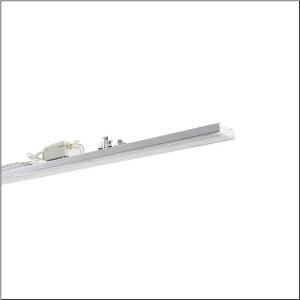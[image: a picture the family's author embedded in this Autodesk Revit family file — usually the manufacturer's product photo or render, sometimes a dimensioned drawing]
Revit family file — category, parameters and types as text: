
# Revit family: licross_r__21_recessed_ho_52te18dn4e5m_8491
name_source: partatom
category: Lighting Fixtures
units: mm (PartAtom-declared; Revit-internal decimal feet)

## family parameters
Cut with Voids When Loaded = No
Host = Face
Light Source = No
Part Type = Normal
Room Calculation Point = No
Round Connector Dimension = Use Diameter
Shared = No

## types (1)
- --- (1 x LED, 14850 lm, 84.6 W, 4000K)
    Apparent Load = 85 VA
    CIE Flux Codes = 75 94 99 100 100
    Color Rendering = 80
    Color Temperature = 4000K
    Default Elevation = 1800 mm
    Description = Licross® 21 Recessed HO, luminaire insert, of sheet steel, galvanised, coil coated, white, length: 1.500mm, width: 66mm, height: 67mm, LED rated luminous flux: 14.850lm, light colour: 840, control gear: DALI 2, with plug, 5-pole, with phase selection, mains connection: 220..240V, AC, 50/60Hz, rated input power: 85W, halogen-free wiring, primary light control with lens, of plastic, primary optical cover: cover, of PMMA, light emission: direct distribution, primary light characteristic: symmetric, protection rating (complete): IP54, insulation class (complete): insulation class I (protective earthing), certification: CE, ENEC, VDE, UKCA, protection symbol: D if used in an environment with non-conductive dust loads with corresponding accessories, impact resistance: IK06, permissible ambient temperature for indoor applications: -25..+30°C, corresponds to IFS (International Featured Standards) requirements for safety and quality in the food industry, reducing of maximum allowable ambient temperature of 5°C with ceiling mounting, LABS conformity tested according to VDMA 24364:2018-05, packaging unit: 1 piece
    Height = 58 mm
    Lamp = 1 x LED
    Lamp Light Flux = 14850 lm
    Lamp Power = 84.6 W
    Lamp count = 1
    Length = 1500 mm
    Luminous efficacy = 176 lm/W
    Manufacturer = Siteco
    ModVariant = No
    Model = 52TE18DN4E5M
    Mounting Place = Ceiling
    Mounting Type = Pendant
    Number of Poles = 1
    OnlyDefault = Yes
    Power Factor = 1
    Product Name = Licross® 21 Recessed HO
    Product group = luminaire insert
    ProductGroupID = 901
    Protection Class = Protection class I
    Protection Degree = IP 54
    RLX_Detail_Level = 1
    RLX_Emergency_Light_Flux = 0 lm
    RLX_Emergency_Type = 0
    RLX_Emergency_Type_DB = No
    RlxData = <blob elided: 24689 chars, md5=0f8bc2dd>
    Socket = socket
    Standby Power = 0 W
    System Light Flux = 14850 lm
    System Power = 85 W
    Type Comments = factory setting: luminous flux: 100 % | dim-lin: 254 | 484 mA
    Type Image = l_1296930.jpg
    URL = http://relux.com
    VarID = @adj_057245
    Voltage = 0 V
    Weight = 0.00 kg
    Width = 66 mm

## geometry (parser evidence)
native form markers: Blend x4, Sweep x12
no freeform markers — native parametric forms only
